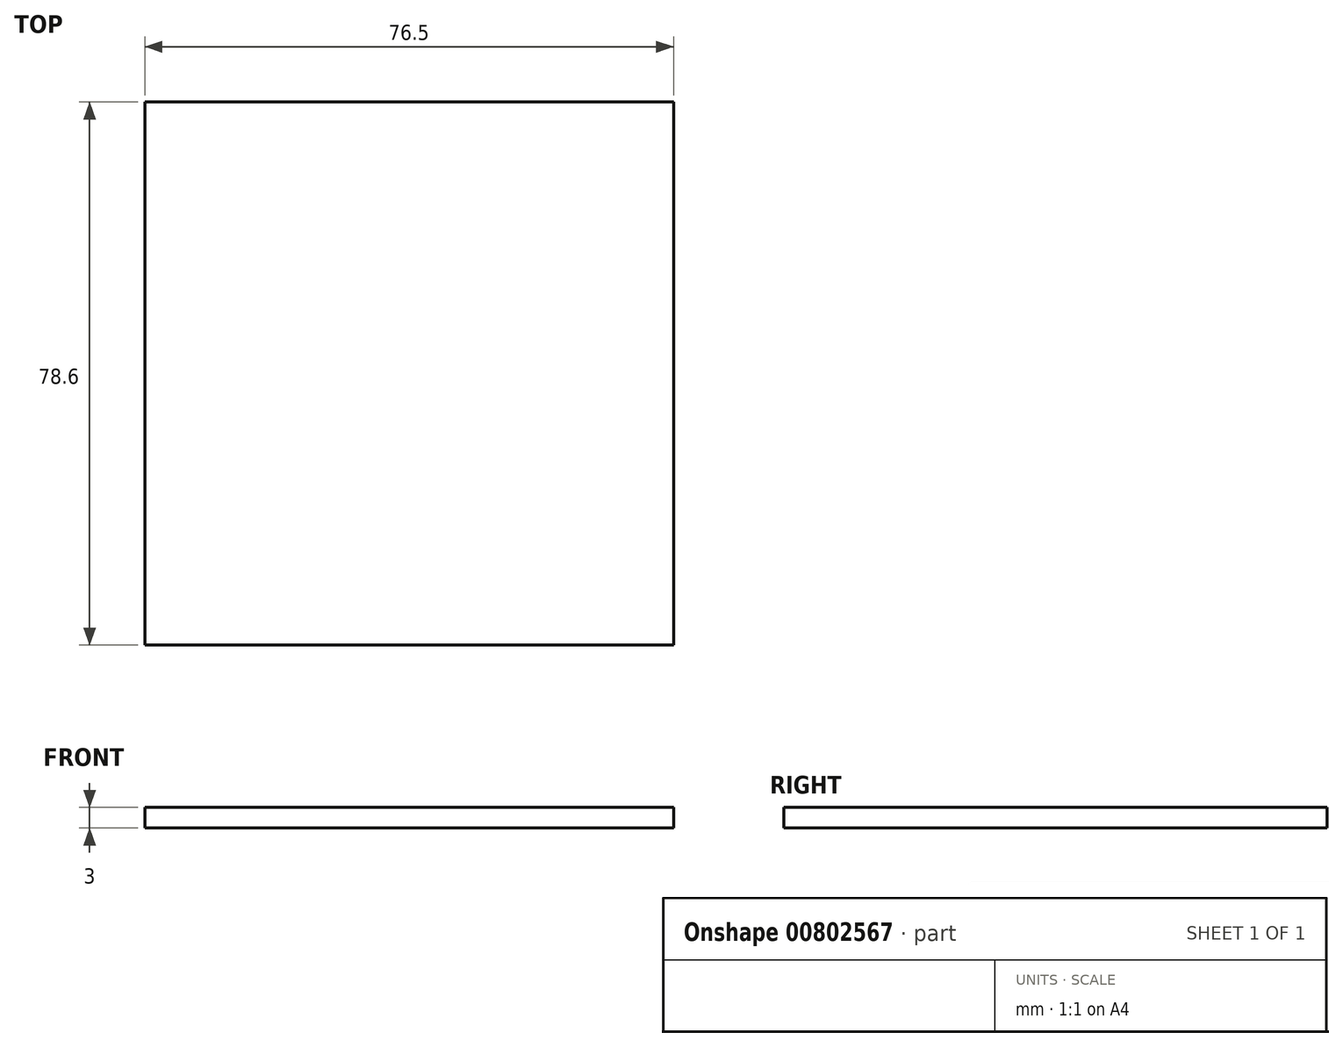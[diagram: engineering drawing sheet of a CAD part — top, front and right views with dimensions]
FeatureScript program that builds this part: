
annotation { "Feature Type Name" : "Feature", "Feature Type Description" : "" }
export const myFeature = defineFeature(function(context is Context, id is Id, definition is map)
    precondition{}
    {
        {
            var Q0;
            Q0=qCreatedBy(makeId("Top.planeOp"),FACE);
            var sketch = newSketch(context, id + "F0", { "sketchPlane" : qUnion([Q0])});
            skLineSegment(sketch, "E0", {"start": v(0, 0) * mm, "end": v(0, 78.6) * mm});
            skLineSegment(sketch, "E1", {"start": v(0, 78.6) * mm, "end": v(-76.5, 78.6) * mm});
            skLineSegment(sketch, "E2", {"start": v(-76.5, 78.6) * mm, "end": v(-76.5, 0) * mm});
            skLineSegment(sketch, "E3", {"start": v(-76.5, 0) * mm, "end": v(0, 0) * mm});
            skSolve(sketch);
        }
        {
            var Q0;
            Q0 = qSketchRegion(id + "F0", true);
            extrude(context, id + "F1", {"entities" : qUnion([Q0]), "depth" : 3 * mm, "offsetDistance" : 25 * mm});
        }
    });
